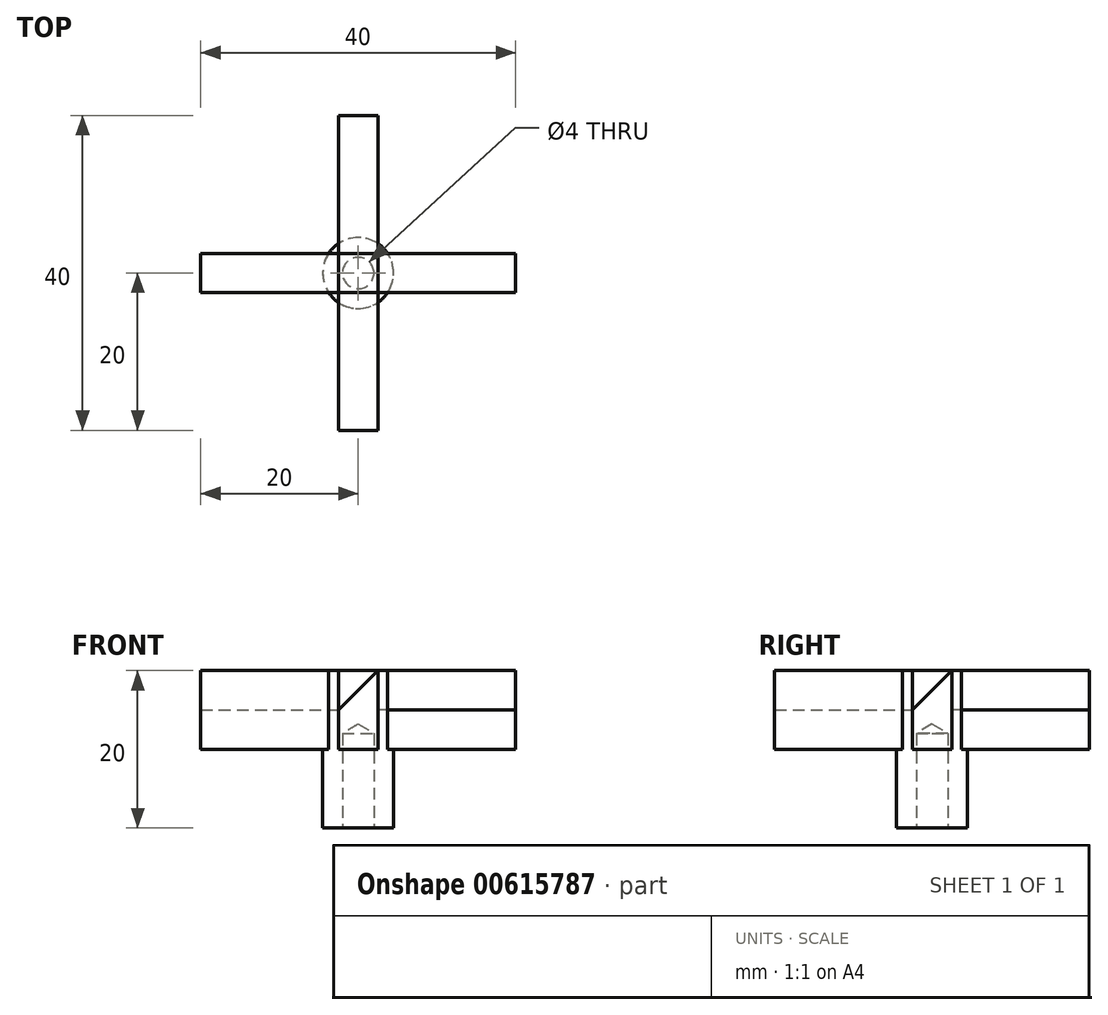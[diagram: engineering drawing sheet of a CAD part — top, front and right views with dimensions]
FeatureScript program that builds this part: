
annotation { "Feature Type Name" : "Feature", "Feature Type Description" : "" }
export const myFeature = defineFeature(function(context is Context, id is Id, definition is map)
    precondition{}
    {
        {
            var Q0;
            Q0=qCreatedBy(makeId("Top.planeOp"),FACE);
            var sketch = newSketch(context, id + "F0", { "sketchPlane" : qUnion([Q0])});
            skCircle(sketch, "E0", {"center": v(0, 0) * mm, "radius": 4.5 * mm});
            skSolve(sketch);
        }
        {
            var Q0;
            Q0=makeQuery(id+"F0.imprint","IMPRINT",FACE,{"disambiguationData":[TD([[makeQuery(id+"F0.imprint","IMPRINT",EDGE,{"derivedFrom":sQuery(id+"F0.wireOp",EDGE,"E0")}),1.0]])]});
            extrude(context, id + "F1", {"entities" : qUnion([Q0]), "depth" : 10 * mm, "offsetDistance" : 25 * mm});
        }
        {
            var Q0;
            Q0=makeQuery(id+"F1.opExtrude","CAP_FACE",FACE,{"disambiguationData":[OSD([sQuery(id+"F0.wireOp",EDGE,"E0")])],"isStart":false});
            var sketch = newSketch(context, id + "F2", { "sketchPlane" : qUnion([Q0])});
            skLineSegment(sketch, "E1.bottom", {"start": v(-20, 2.5) * mm, "end": v(20, 2.5) * mm});
            skLineSegment(sketch, "E1.top", {"start": v(-20, -2.5) * mm, "end": v(20, -2.5) * mm});
            skLineSegment(sketch, "E1.left", {"start": v(-20, 2.5) * mm, "end": v(-20, -2.5) * mm});
            skLineSegment(sketch, "E1.right", {"start": v(20, 2.5) * mm, "end": v(20, -2.5) * mm});
            skPoint(sketch, "E1.middle", {"position": v(0, 0) * mm});
            skLineSegment(sketch, "E2.bottom", {"start": v(-2.5, 20) * mm, "end": v(2.5, 20) * mm});
            skLineSegment(sketch, "E2.top", {"start": v(-2.5, -20) * mm, "end": v(2.5, -20) * mm});
            skLineSegment(sketch, "E2.left", {"start": v(-2.5, 20) * mm, "end": v(-2.5, -20) * mm});
            skLineSegment(sketch, "E2.right", {"start": v(2.5, 20) * mm, "end": v(2.5, -20) * mm});
            skSolve(sketch);
        }
        {
            var Q0;
            {var subQ0=sQuery(id+"F2.wireOp",EDGE,"E2.top");Q0=makeQuery(id+"F2.imprint","IMPRINT",FACE,{"disambiguationData":[TD([[makeQuery(id+"F2.imprint","IMPRINT",EDGE,{"derivedFrom":subQ0}),1.0]])]});}
            var Q1;
            {var subQ0=sQuery(id+"F2.wireOp",EDGE,"E1.left");Q1=makeQuery(id+"F2.imprint","IMPRINT",FACE,{"disambiguationData":[TD([[makeQuery(id+"F2.imprint","IMPRINT",EDGE,{"derivedFrom":subQ0}),1.0]])]});}
            var Q2;
            {var subQ0=sQuery(id+"F2.wireOp",EDGE,"E2.bottom");Q2=makeQuery(id+"F2.imprint","IMPRINT",FACE,{"disambiguationData":[TD([[makeQuery(id+"F2.imprint","IMPRINT",EDGE,{"derivedFrom":subQ0}),-1.0]])]});}
            var Q3;
            {var subQ0=sQuery(id+"F2.wireOp",EDGE,"E1.right");Q3=makeQuery(id+"F2.imprint","IMPRINT",FACE,{"disambiguationData":[TD([[makeQuery(id+"F2.imprint","IMPRINT",EDGE,{"derivedFrom":subQ0}),-1.0]])]});}
            var Q4;
            {var subQ0=sQuery(id+"F2.wireOp",EDGE,"E2.right");var subQ1=sQuery(id+"F2.wireOp",EDGE,"E1.bottom");var subQ2=makeQuery(id+"F2.imprint","INTERSECT",VERTEX,{"derivedFrom":[subQ1,subQ0]});Q4=makeQuery(id+"F2.imprint","IMPRINT",FACE,{"disambiguationData":[TD([[makeQuery(id+"F2.imprint","IMPRINT",EDGE,{"disambiguationData":[TD([[subQ2,-1.0]])],"derivedFrom":subQ1}),-1.0]])]});}
            var Q5;
            {var subQ0=sQuery(id+"F2.wireOp",EDGE,"E2.left");var subQ1=sQuery(id+"F2.wireOp",EDGE,"E1.bottom");var subQ2=makeQuery(id+"F2.imprint","INTERSECT",VERTEX,{"derivedFrom":[subQ1,subQ0]});Q5=makeQuery(id+"F2.imprint","IMPRINT",FACE,{"disambiguationData":[TD([[makeQuery(id+"F2.imprint","IMPRINT",EDGE,{"disambiguationData":[TD([[subQ2,-1.0]])],"derivedFrom":subQ1}),-1.0]])]});}
            var Q6;
            {var subQ0=sQuery(id+"F2.wireOp",EDGE,"E2.left");var subQ1=sQuery(id+"F2.wireOp",EDGE,"E1.top");var subQ2=makeQuery(id+"F2.imprint","INTERSECT",VERTEX,{"derivedFrom":[subQ1,subQ0]});Q6=makeQuery(id+"F2.imprint","IMPRINT",FACE,{"disambiguationData":[TD([[makeQuery(id+"F2.imprint","IMPRINT",EDGE,{"disambiguationData":[TD([[subQ2,-1.0]])],"derivedFrom":subQ1}),-1.0]])]});}
            var Q7;
            {var subQ0=sQuery(id+"F2.wireOp",EDGE,"E2.left");var subQ1=sQuery(id+"F2.wireOp",EDGE,"E1.bottom");var subQ2=makeQuery(id+"F2.imprint","INTERSECT",VERTEX,{"derivedFrom":[subQ1,subQ0]});Q7=makeQuery(id+"F2.imprint","IMPRINT",FACE,{"disambiguationData":[TD([[makeQuery(id+"F2.imprint","IMPRINT",EDGE,{"disambiguationData":[TD([[subQ2,1.0]])],"derivedFrom":subQ1}),-1.0]])]});}
            var Q8;
            {var subQ0=sQuery(id+"F2.wireOp",EDGE,"E2.left");var subQ1=sQuery(id+"F2.wireOp",EDGE,"E1.bottom");var subQ2=makeQuery(id+"F2.imprint","INTERSECT",VERTEX,{"derivedFrom":[subQ1,subQ0]});Q8=makeQuery(id+"F2.imprint","IMPRINT",FACE,{"disambiguationData":[TD([[makeQuery(id+"F2.imprint","IMPRINT",EDGE,{"disambiguationData":[TD([[subQ2,-1.0]])],"derivedFrom":subQ1}),1.0]])]});}
            extrude(context, id + "F3", {"entities" : qUnion([Q0, Q1, Q2, Q3, Q4, Q5, Q6, Q7, Q8]), "operationType" : NewBodyOperationType.ADD, "depth" : 10 * mm, "offsetDistance" : 25 * mm});
        }
        {
            var Q0;
            {var subQ0=sQuery(id+"F2.wireOp",EDGE,"E2.left");Q0=makeQuery(id+"F3.opExtrude","CAP_EDGE",EDGE,{"disambiguationData":[OSD([subQ0]),TDD([makeQuery(id+"F2.imprint","IMPRINT",EDGE,{"disambiguationData":[TD([[makeQuery(id+"F2.imprint","INTERSECT",VERTEX,{"derivedFrom":[sQuery(id+"F2.wireOp",EDGE,"E1.top"),subQ0]}),-1.0]])],"derivedFrom":subQ0}),makeQuery(id+"F2.imprint","IMPRINT",EDGE,{"disambiguationData":[TD([[makeQuery(id+"F2.imprint","INTERSECT",VERTEX,{"derivedFrom":[sQuery(id+"F2.wireOp",EDGE,"E2.top"),subQ0]}),1.0]])],"derivedFrom":subQ0})])],"isStart":false});}
            var Q1;
            {var subQ0=sQuery(id+"F2.wireOp",EDGE,"E1.bottom");Q1=makeQuery(id+"F3.opExtrude","CAP_EDGE",EDGE,{"disambiguationData":[OSD([subQ0]),TDD([makeQuery(id+"F2.imprint","IMPRINT",EDGE,{"disambiguationData":[TD([[makeQuery(id+"F2.imprint","INTERSECT",VERTEX,{"derivedFrom":[subQ0,sQuery(id+"F2.wireOp",EDGE,"E1.left")]}),-1.0]])],"derivedFrom":subQ0}),makeQuery(id+"F2.imprint","IMPRINT",EDGE,{"disambiguationData":[TD([[makeQuery(id+"F2.imprint","INTERSECT",VERTEX,{"derivedFrom":[subQ0,sQuery(id+"F2.wireOp",EDGE,"E2.left")]}),1.0]])],"derivedFrom":subQ0})])],"isStart":false});}
            var Q2;
            {var subQ0=sQuery(id+"F2.wireOp",EDGE,"E2.right");Q2=makeQuery(id+"F3.opExtrude","CAP_EDGE",EDGE,{"disambiguationData":[OSD([subQ0]),TDD([makeQuery(id+"F2.imprint","IMPRINT",EDGE,{"disambiguationData":[TD([[makeQuery(id+"F2.imprint","INTERSECT",VERTEX,{"derivedFrom":[sQuery(id+"F2.wireOp",EDGE,"E2.bottom"),subQ0]}),-1.0]])],"derivedFrom":subQ0}),makeQuery(id+"F2.imprint","IMPRINT",EDGE,{"disambiguationData":[TD([[makeQuery(id+"F2.imprint","INTERSECT",VERTEX,{"derivedFrom":[sQuery(id+"F2.wireOp",EDGE,"E1.bottom"),subQ0]}),1.0]])],"derivedFrom":subQ0})])],"isStart":false});}
            var Q3;
            {var subQ0=sQuery(id+"F2.wireOp",EDGE,"E1.top");Q3=makeQuery(id+"F3.opExtrude","CAP_EDGE",EDGE,{"disambiguationData":[OSD([subQ0]),TDD([makeQuery(id+"F2.imprint","IMPRINT",EDGE,{"disambiguationData":[TD([[makeQuery(id+"F2.imprint","INTERSECT",VERTEX,{"derivedFrom":[subQ0,sQuery(id+"F2.wireOp",EDGE,"E2.right")]}),-1.0]])],"derivedFrom":subQ0}),makeQuery(id+"F2.imprint","IMPRINT",EDGE,{"disambiguationData":[TD([[makeQuery(id+"F2.imprint","INTERSECT",VERTEX,{"derivedFrom":[subQ0,sQuery(id+"F2.wireOp",EDGE,"E1.right")]}),1.0]])],"derivedFrom":subQ0})])],"isStart":false});}
            chamfer(context, id + "F4", {"entities" : qUnion([Q0, Q1, Q2, Q3]), "width" : 5 * mm, "tangentPropagation" : true});
        }
        {
            var Q0;
            {var subQ0=sQuery(id+"F0.wireOp",EDGE,"E0");var subQ1=sQuery(id+"F2.wireOp",EDGE,"E2.left");var subQ2=sQuery(id+"F2.wireOp",EDGE,"E1.bottom");var subQ3=makeQuery(id+"F2.imprint","INTERSECT",VERTEX,{"derivedFrom":[subQ2,subQ1]});var subQ6=sQuery(id+"F2.wireOp",EDGE,"E1.left");Q0=makeQuery(id+"F3.boolean.opBoolean","SPLIT",FACE,{"disambiguationData":[TD([makeQuery(id+"F3.opExtrude","SWEPT_FACE",FACE,{"disambiguationData":[OSD([subQ2]),TDD([makeQuery(id+"F2.imprint","IMPRINT",EDGE,{"disambiguationData":[TD([[makeQuery(id+"F2.imprint","INTERSECT",VERTEX,{"derivedFrom":[subQ2,subQ6]}),-1.0]])],"derivedFrom":subQ2}),makeQuery(id+"F2.imprint","IMPRINT",EDGE,{"disambiguationData":[TD([[subQ3,1.0]])],"derivedFrom":subQ2})])]})])],"derivedFrom":makeQuery(id+"F1.opExtrude","CAP_FACE",FACE,{"disambiguationData":[OSD([subQ0])],"isStart":false})});}
            var Q1;
            {var subQ0=sQuery(id+"F0.wireOp",EDGE,"E0");var subQ1=sQuery(id+"F2.wireOp",EDGE,"E2.right");var subQ2=sQuery(id+"F2.wireOp",EDGE,"E1.bottom");var subQ3=makeQuery(id+"F2.imprint","INTERSECT",VERTEX,{"derivedFrom":[subQ2,subQ1]});var subQ7=sQuery(id+"F2.wireOp",EDGE,"E1.right");Q1=makeQuery(id+"F3.boolean.opBoolean","SPLIT",FACE,{"disambiguationData":[TD([makeQuery(id+"F3.opExtrude","SWEPT_FACE",FACE,{"disambiguationData":[OSD([subQ2]),TDD([makeQuery(id+"F2.imprint","IMPRINT",EDGE,{"disambiguationData":[TD([[subQ3,-1.0]])],"derivedFrom":subQ2}),makeQuery(id+"F2.imprint","IMPRINT",EDGE,{"disambiguationData":[TD([[makeQuery(id+"F2.imprint","INTERSECT",VERTEX,{"derivedFrom":[subQ2,subQ7]}),1.0]])],"derivedFrom":subQ2})])]})])],"derivedFrom":makeQuery(id+"F1.opExtrude","CAP_FACE",FACE,{"disambiguationData":[OSD([subQ0])],"isStart":false})});}
            var Q2;
            {var subQ0=sQuery(id+"F0.wireOp",EDGE,"E0");var subQ1=sQuery(id+"F2.wireOp",EDGE,"E2.right");var subQ3=sQuery(id+"F2.wireOp",EDGE,"E1.right");var subQ4=sQuery(id+"F2.wireOp",EDGE,"E1.top");var subQ7=makeQuery(id+"F2.imprint","INTERSECT",VERTEX,{"derivedFrom":[subQ4,subQ1]});Q2=makeQuery(id+"F3.boolean.opBoolean","SPLIT",FACE,{"disambiguationData":[TD([makeQuery(id+"F3.opExtrude","SWEPT_FACE",FACE,{"disambiguationData":[OSD([subQ4]),TDD([makeQuery(id+"F2.imprint","IMPRINT",EDGE,{"disambiguationData":[TD([[subQ7,-1.0]])],"derivedFrom":subQ4}),makeQuery(id+"F2.imprint","IMPRINT",EDGE,{"disambiguationData":[TD([[makeQuery(id+"F2.imprint","INTERSECT",VERTEX,{"derivedFrom":[subQ4,subQ3]}),1.0]])],"derivedFrom":subQ4})])]})])],"derivedFrom":makeQuery(id+"F1.opExtrude","CAP_FACE",FACE,{"disambiguationData":[OSD([subQ0])],"isStart":false})});}
            var Q3;
            {var subQ0=sQuery(id+"F0.wireOp",EDGE,"E0");var subQ1=sQuery(id+"F2.wireOp",EDGE,"E2.left");var subQ3=sQuery(id+"F2.wireOp",EDGE,"E1.left");var subQ4=sQuery(id+"F2.wireOp",EDGE,"E1.top");var subQ7=makeQuery(id+"F2.imprint","INTERSECT",VERTEX,{"derivedFrom":[subQ4,subQ1]});Q3=makeQuery(id+"F3.boolean.opBoolean","SPLIT",FACE,{"disambiguationData":[TD([makeQuery(id+"F3.opExtrude","SWEPT_FACE",FACE,{"disambiguationData":[OSD([subQ4]),TDD([makeQuery(id+"F2.imprint","IMPRINT",EDGE,{"disambiguationData":[TD([[makeQuery(id+"F2.imprint","INTERSECT",VERTEX,{"derivedFrom":[subQ4,subQ3]}),-1.0]])],"derivedFrom":subQ4}),makeQuery(id+"F2.imprint","IMPRINT",EDGE,{"disambiguationData":[TD([[subQ7,1.0]])],"derivedFrom":subQ4})])]})])],"derivedFrom":makeQuery(id+"F1.opExtrude","CAP_FACE",FACE,{"disambiguationData":[OSD([subQ0])],"isStart":false})});}
            extrude(context, id + "F5", {"entities" : qUnion([Q0, Q1, Q2, Q3]), "operationType" : NewBodyOperationType.ADD, "depth" : 10 * mm, "offsetDistance" : 25 * mm});
        }
        {
            var Q0;
            Q0=makeQuery(id+"F1.opExtrude","CAP_FACE",FACE,{"disambiguationData":[OSD([sQuery(id+"F0.wireOp",EDGE,"E0")])],"isStart":true});
            var sketch = newSketch(context, id + "F6", { "sketchPlane" : qUnion([Q0])});
            skPoint(sketch, "E3", {"position": v(0, 0) * mm});
            skSolve(sketch);
        }
        {
            var Q0;
            Q0=sQuery(id+"F6.wireOp",VERTEX,"E3");
            var Q1;
            Q1=makeQuery(id+"F1.opExtrude","SWEPT_BODY",BODY,{"disambiguationData":[OSD([sQuery(id+"F0.wireOp",EDGE,"E0")])]});
            hole(context, id + "F7", {"style" : HoleStyle.SIMPLE, "endStyle" : HoleEndStyle.BLIND, "holeDiameter" : 4 * mm, "majorDiameter" : 5 * mm, "holeDepth" : 12 * mm, "isTappedThrough" : true, "tappedDepth" : 12 * mm, "tapClearance" : 3, "locations" : qUnion([Q0]), "scope" : qUnion([Q1])});
        }
    });
